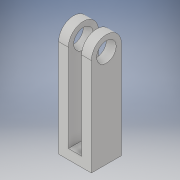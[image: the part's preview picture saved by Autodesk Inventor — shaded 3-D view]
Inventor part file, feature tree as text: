
AUTODESK INVENTOR PART (.ipt)
format: ipt  version: 2017 (Build 210142000, 142)  size: 122,880 bytes
history: native  units: in
note: dims shown in document units (in); Inventor stores cm internally (conversion verified against a paired STEP export)
features: extrude x2, sketch x2, projected_geometry x2
ambient origin geometry x8: Origin, YZ Plane, XZ Plane, XY Plane, X Axis, Y Axis, Z Axis, Center Point
bodies: Solid1 (feature_tree)
feature tree (6):
  extrude  "Extrusion1"  Depth=0.84in TaperAngle=0.0deg
  extrude  "Extrusion2"  Depth=0.25in
  sketch  "Sketch1"  dims[d0=0.5in d1=0.77in d2=2.5in d3=0.77in d4=0.84in d5=0.0in]
  sketch  "Sketch2"  dims[d7=0.25in d8=0.25in d9=0.84in d10=0.0in d11=0.25in]
  projected_geometry  "Projected Loop1"
  projected_geometry  "Projected Loop2"
